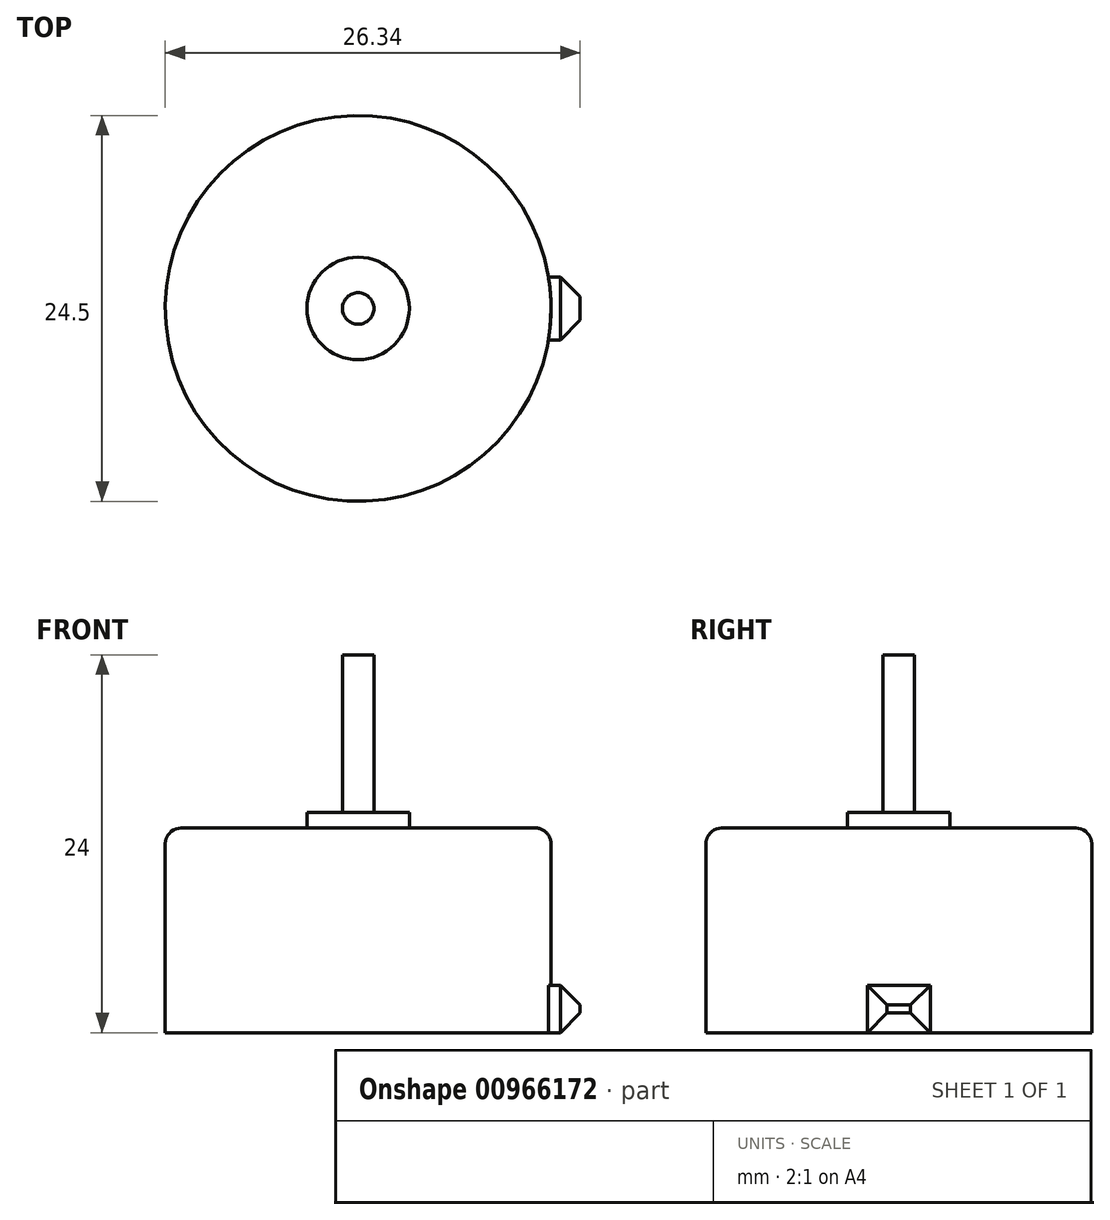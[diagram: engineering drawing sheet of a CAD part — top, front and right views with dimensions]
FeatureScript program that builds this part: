
annotation { "Feature Type Name" : "Feature", "Feature Type Description" : "" }
export const myFeature = defineFeature(function(context is Context, id is Id, definition is map)
    precondition{}
    {
        {
            var Q0;
            Q0=qCreatedBy(makeId("Top.planeOp"),FACE);
            var sketch = newSketch(context, id + "F0", { "sketchPlane" : qUnion([Q0])});
            skCircle(sketch, "E0", {"center": v(0, 0) * mm, "radius": 12.25 * mm});
            skCircle(sketch, "E1", {"center": v(0, 0) * mm, "radius": 3.25 * mm});
            skCircle(sketch, "E2", {"center": v(0, 0) * mm, "radius": 1 * mm});
            skLineSegment(sketch, "E3.bottom", {"start": v(12.09, 2) * mm, "end": v(14.09, 2) * mm});
            skLineSegment(sketch, "E3.top", {"start": v(12.09, -2) * mm, "end": v(14.09, -2) * mm});
            skLineSegment(sketch, "E3.right", {"start": v(14.09, 2) * mm, "end": v(14.09, -2) * mm});
            skSolve(sketch);
        }
        {
            var Q0;
            Q0=makeQuery(id+"F0.imprint","IMPRINT",FACE,{"disambiguationData":[TD([[makeQuery(id+"F0.imprint","IMPRINT",EDGE,{"derivedFrom":sQuery(id+"F0.wireOp",EDGE,"E1")}),-1.0]])]});
            extrude(context, id + "F1", {"entities" : qUnion([Q0]), "depth" : 13 * mm, "offsetDistance" : 25 * mm});
        }
        {
            var Q0;
            Q0=makeQuery(id+"F0.imprint","IMPRINT",FACE,{"disambiguationData":[TD([[makeQuery(id+"F0.imprint","IMPRINT",EDGE,{"derivedFrom":sQuery(id+"F0.wireOp",EDGE,"E1")}),1.0]])]});
            extrude(context, id + "F2", {"entities" : qUnion([Q0]), "operationType" : NewBodyOperationType.ADD, "depth" : 14 * mm, "offsetDistance" : 25 * mm});
        }
        {
            var Q0;
            Q0=makeQuery(id+"F0.imprint","IMPRINT",FACE,{"disambiguationData":[TD([[makeQuery(id+"F0.imprint","IMPRINT",EDGE,{"derivedFrom":sQuery(id+"F0.wireOp",EDGE,"E2")}),1.0]])]});
            extrude(context, id + "F3", {"entities" : qUnion([Q0]), "operationType" : NewBodyOperationType.ADD, "depth" : 24 * mm, "offsetDistance" : 25 * mm});
        }
        {
            var Q0;
            {var subQ0=sQuery(id+"F0.wireOp",EDGE,"E3.bottom");Q0=makeQuery(id+"F0.imprint","IMPRINT",FACE,{"disambiguationData":[TD([[makeQuery(id+"F0.imprint","IMPRINT",EDGE,{"derivedFrom":subQ0}),-1.0]])]});}
            extrude(context, id + "F4", {"entities" : qUnion([Q0]), "operationType" : NewBodyOperationType.ADD, "depth" : 3 * mm, "offsetDistance" : 25 * mm});
        }
        {
            var Q0;
            Q0=makeQuery(id+"F1.opExtrude","CAP_EDGE",EDGE,{"disambiguationData":[OSD([sQuery(id+"F0.wireOp",EDGE,"E0")])],"isStart":false});
            fillet(context, id + "F5", {"entities" : qUnion([Q0]), "radius" : 1 * mm, "tangentPropagation" : true, "allowEdgeOverflow" : false});
        }
        {
            var Q0;
            Q0=makeQuery(id+"F4.opExtrude","SWEPT_FACE",FACE,{"disambiguationData":[OSD([sQuery(id+"F0.wireOp",EDGE,"E3.right")])]});
            chamfer(context, id + "F6", {"entities" : qUnion([Q0]), "width" : 1.25 * mm, "tangentPropagation" : true});
        }
    });
